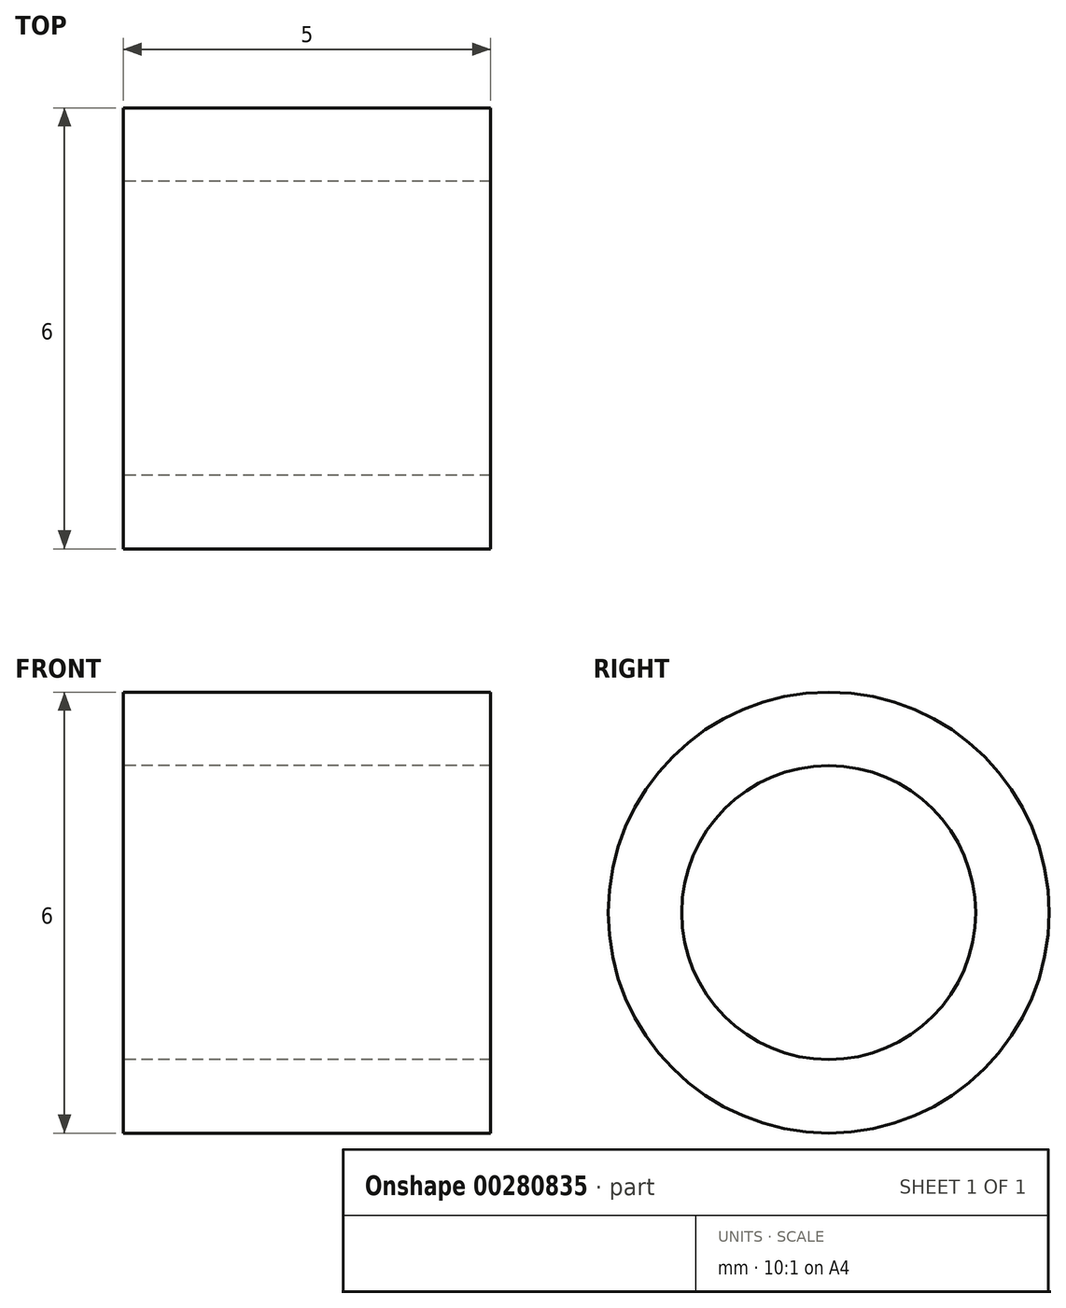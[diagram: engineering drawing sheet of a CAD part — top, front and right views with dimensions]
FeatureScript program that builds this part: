
annotation { "Feature Type Name" : "Feature", "Feature Type Description" : "" }
export const myFeature = defineFeature(function(context is Context, id is Id, definition is map)
    precondition{}
    {
        {
            var Q0;
            Q0=qCreatedBy(makeId("Front.planeOp"),FACE);
            var sketch = newSketch(context, id + "F0", { "sketchPlane" : qUnion([Q0])});
            skLineSegment(sketch, "E0.bottom", {"start": v(-2.5, 3) * mm, "end": v(2.5, 3) * mm});
            skLineSegment(sketch, "E0.top", {"start": v(-2.5, 2) * mm, "end": v(2.5, 2) * mm});
            skLineSegment(sketch, "E0.left", {"start": v(-2.5, 3) * mm, "end": v(-2.5, 2) * mm});
            skLineSegment(sketch, "E0.right", {"start": v(2.5, 3) * mm, "end": v(2.5, 2) * mm});
            skLineSegment(sketch, "E1", {"start": v(-4.62, 0) * mm, "end": v(4.08, 0) * mm, "construction": true});
            skSolve(sketch);
        }
        {
            var Q0;
            Q0=makeQuery(id+"F0.imprint","IMPRINT",FACE,{"disambiguationData":[TD([[makeQuery(id+"F0.imprint","IMPRINT",EDGE,{"derivedFrom":sQuery(id+"F0.wireOp",EDGE,"E0.bottom")}),-1.0]])]});
            var Q1;
            Q1=sQuery(id+"F0.wireOp",EDGE,"E1");
            revolve(context, id + "F1", {"entities" : qUnion([Q0]), "axis" : qUnion([Q1]), "revolveType" : RevolveType.FULL});
        }
    });
